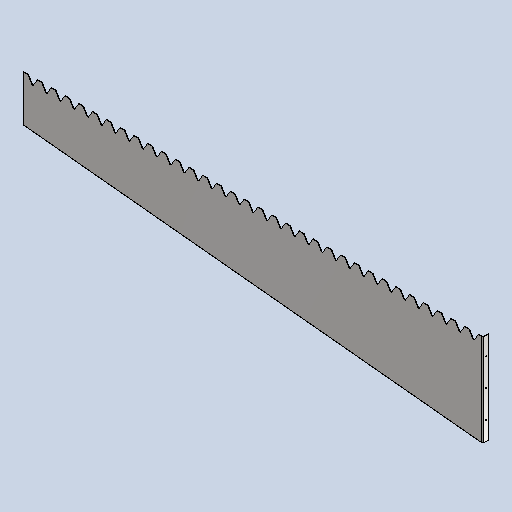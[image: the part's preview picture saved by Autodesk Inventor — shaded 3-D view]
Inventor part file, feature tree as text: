
AUTODESK INVENTOR PART (.ipt)
format: ipt  version: 2025 (Build 290162010, 162A)  size: 663,552 bytes
history: native  units: mm
features: other x6, sheet_metal_op x4, sketch x4, reference x3, extrude x2, fillet x1, pattern_linear x1
ambient origin geometry x8: Origin, YZ Plane, XZ Plane, XY Plane, X Axis, Y Axis, Z Axis, Center Point
bodies: Solid1 (feature_tree)
feature tree (21):
  sheet_metal_op  "Face1"
  extrude  "Extrusion2"  Depth=2000.0mm
  fillet  "Fillet2"  Radius=200.0mm
  pattern_linear  "Rectangular Pattern1"  Count1=4  [1 undecoded]
  sheet_metal_op  "Flange1"
  extrude  "Extrusion3"  Depth=30.0mm
  other  "A-Side Definition"
  sketch  "Sketch1"  dims[d0=400.0mm d1=2000.0mm d2=200.0mm]
  other  "Plate1"
  sketch  "Sketch3"  dims[d3=2.0mm]
  sketch  "Sketch4"  dims[d4=10.0mm]
  other  "Plate2"
  sheet_metal_op  "Bend1"
  sheet_metal_op  "Corner1"
  sketch  "Sketch6"  dims[d12=5.0mm d13=40.0mm d14=30.0mm d15=20.0mm d16=0.0mm d17=0.0mm d18=2.0mm d19=330.0mm d21=60.0mm d22=2.0mm d23=1.0mm d24=4.0mm d25=2.75mm d26=25.0mm d27=90.0deg d28=2.75mm d29=8.0mm d30=2.0mm d31=2.75mm d36=0.0mm d37=0.0mm]
  reference  "Reference2"
  reference  "Reference3"
  reference  "Reference4"
  other  "ASY MSC 001 отстойник осветлитель.iam"
  other  "MSC 073 ridge 3.ipt:1"
  other  "Definition1"
note: 1 required parameter value undecoded (feature->parameter linkage not recoverable at this tier; creation-order binding heuristic only, values carry confidence <= 0.55)
